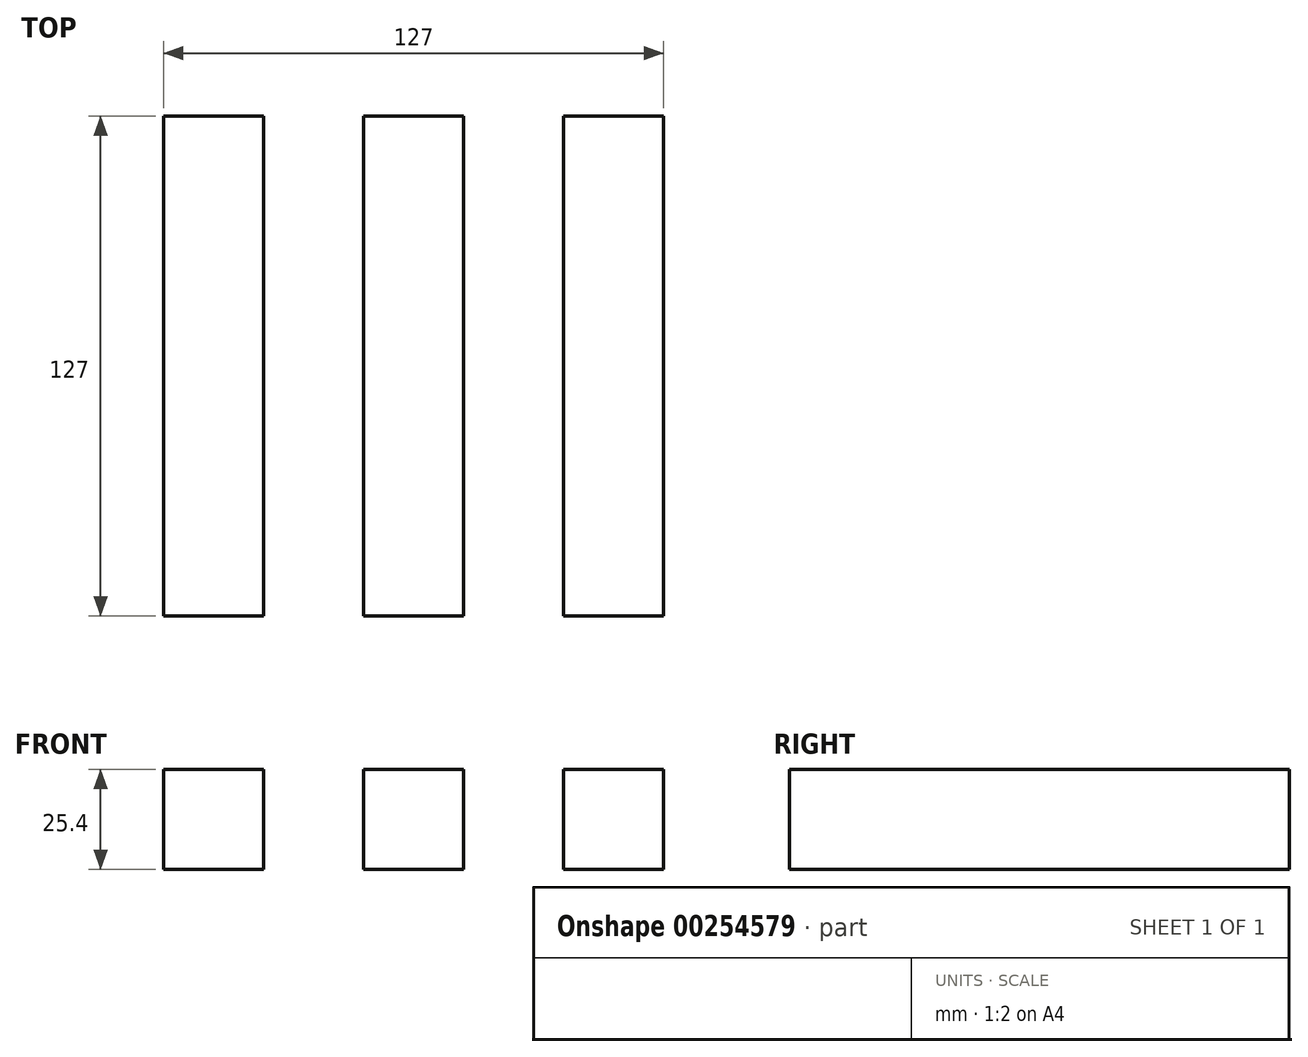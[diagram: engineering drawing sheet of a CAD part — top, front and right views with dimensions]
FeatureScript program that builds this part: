
annotation { "Feature Type Name" : "Feature", "Feature Type Description" : "" }
export const myFeature = defineFeature(function(context is Context, id is Id, definition is map)
    precondition{}
    {
        {
            var Q0;
            Q0=qCreatedBy(makeId("Front.planeOp"),FACE);
            var sketch = newSketch(context, id + "F0", { "sketchPlane" : qUnion([Q0])});
            skLineSegment(sketch, "E0", {"start": v(0, 0) * mm, "end": v(-51.16, 0) * mm});
            skLineSegment(sketch, "E1.bottom", {"start": v(-63.86, 12.7) * mm, "end": v(-38.46, 12.7) * mm});
            skLineSegment(sketch, "E1.top", {"start": v(-63.86, -12.7) * mm, "end": v(-38.46, -12.7) * mm});
            skLineSegment(sketch, "E1.left", {"start": v(-63.86, 12.7) * mm, "end": v(-63.86, -12.7) * mm});
            skLineSegment(sketch, "E1.right", {"start": v(-38.46, 12.7) * mm, "end": v(-38.46, -12.7) * mm});
            skPoint(sketch, "E1.middle", {"position": v(-51.16, 0) * mm});
            skPoint(sketch, "E2.middle", {"position": v(0, 0) * mm});
            skPoint(sketch, "E2.right.start.orphan", {"position": v(12.17, 12.35) * mm});
            skPoint(sketch, "E2.top.end.orphan", {"position": v(13.06, -12.7) * mm});
            skPoint(sketch, "E3.orphan", {"position": v(-12.17, -12.35) * mm});
            skPoint(sketch, "E2.left.start.orphan", {"position": v(-13.06, 12.7) * mm});
            skLineSegment(sketch, "E4", {"start": v(-51.16, 0) * mm, "end": v(-0.36, 0) * mm});
            skLineSegment(sketch, "E5.bottom", {"start": v(-13.06, 12.7) * mm, "end": v(12.34, 12.7) * mm});
            skLineSegment(sketch, "E5.top", {"start": v(-13.06, -12.7) * mm, "end": v(12.34, -12.7) * mm});
            skLineSegment(sketch, "E5.left", {"start": v(-13.06, 12.7) * mm, "end": v(-13.06, -12.7) * mm});
            skLineSegment(sketch, "E5.right", {"start": v(12.34, 12.7) * mm, "end": v(12.34, -12.7) * mm});
            skPoint(sketch, "E5.middle", {"position": v(-0.36, 0) * mm});
            skLineSegment(sketch, "E6", {"start": v(-0.36, 0) * mm, "end": v(50.44, 0) * mm});
            skLineSegment(sketch, "E7.bottom", {"start": v(37.74, 12.7) * mm, "end": v(63.14, 12.7) * mm});
            skLineSegment(sketch, "E7.top", {"start": v(37.74, -12.7) * mm, "end": v(63.14, -12.7) * mm});
            skLineSegment(sketch, "E7.left", {"start": v(37.74, 12.7) * mm, "end": v(37.74, -12.7) * mm});
            skLineSegment(sketch, "E7.right", {"start": v(63.14, 12.7) * mm, "end": v(63.14, -12.7) * mm});
            skPoint(sketch, "E7.middle", {"position": v(50.44, 0) * mm});
            skSolve(sketch);
        }
        {
            var Q0;
            Q0 = qSketchRegion(id + "F0", true);
            extrude(context, id + "F1", {"entities" : qUnion([Q0]), "endBound" : BoundingType.SYMMETRIC, "depth" : 127 * mm});
        }
    });
